# Revit family: Zaniboni-Diva-2_Inch_Aperture_20°-1
name_source: partatom
category: Lighting Fixtures
revit_build: Autodesk Revit 2016 (Build: 20150220_1215(x64)
units: mm (PartAtom-declared; Revit-internal decimal feet)

## family parameters
Cut with Voids When Loaded = No
Host = Face
Light Source = No
Part Type = Normal
Room Calculation Point = No
Round Connector Dimension = Use Diameter
Shared = No

## types (4) — shared parameters
Assembly Code = E1020300
Beam = 36°
Body Finish = ZBN - Metal Matte White
CRI = 80
Default Elevation = 1"
Diffuser Finish = ZBN - Metal Matte White
Frame Finish = ZBN - Metal Matte White
Kelvin = 3000°K
Keynote = 12500
Manufacturer = Zaniboni
Mechanism Finish = ZBN - Plastic-Black
Screen Finish = ZBN - Glass
Support Finish = ZBN - Metal Matte White
Type Comments = Diva
URL = www.zanibonilighting.com
Voltage = 120 V
Wattage Comments = 14W

## per-type parameters (varying)
| type | Description | Length | RD | RQ | RT | SD | SQ | ST | Width |
| D1-DIVTS-0730A-3C-WS | 2 inch 1 Light Sources Adjustable 20° | 2 63/64" | No | No | No | No | No | No | 2 63/64" |
| D1-DIVTD-1430A-3C-WS | 2 inch 2 Light Sources Adjustable 20° | 6" | Yes | No | No | Yes | No | No | 2 63/64" |
| D1-DIVTT-2130A-3C-WS | 2 inch 3 Light Sources Adjustable 20° | 9" | Yes | No | Yes | Yes | No | Yes | 2 63/64" |
| D1-DIVTQ-2830A-3C-WS | 2 inch 4 Light Sources Adjustable 20° | 6" | Yes | Yes | No | Yes | Yes | No | 5 23/32" |

note: column(s) folded — value = type name in every type: Model

## geometry (parser evidence)
native form markers: Sweep x5
no freeform markers — native parametric forms only
